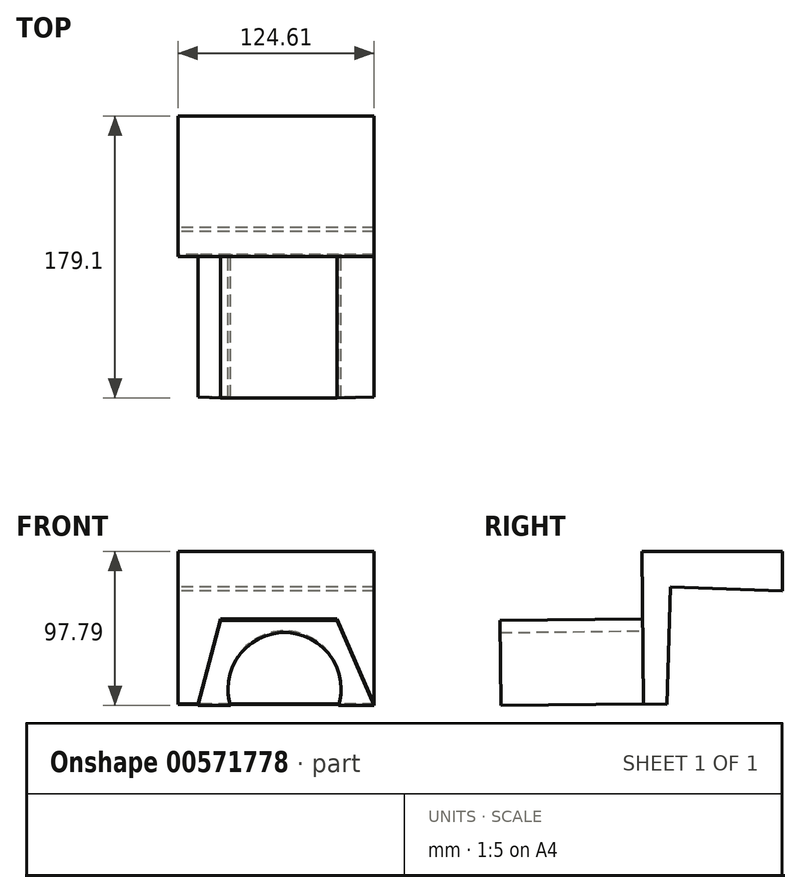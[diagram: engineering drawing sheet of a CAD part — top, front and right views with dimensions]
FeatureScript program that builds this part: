
annotation { "Feature Type Name" : "Feature", "Feature Type Description" : "" }
export const myFeature = defineFeature(function(context is Context, id is Id, definition is map)
    precondition{}
    {
        {
            var Q0;
            Q0=qCreatedBy(makeId("Right.planeOp"),FACE);
            var sketch = newSketch(context, id + "F0", { "sketchPlane" : qUnion([Q0])});
            skLineSegment(sketch, "E0", {"start": v(-40.66, 42.4) * mm, "end": v(48.47, 42.4) * mm});
            skLineSegment(sketch, "E1", {"start": v(48.47, 42.4) * mm, "end": v(48.47, 17.48) * mm});
            skLineSegment(sketch, "E2", {"start": v(48.47, 17.48) * mm, "end": v(-22.34, 19.8) * mm});
            skLineSegment(sketch, "E3", {"start": v(-22.34, 19.8) * mm, "end": v(-24.79, -54.84) * mm});
            skLineSegment(sketch, "E4", {"start": v(-24.79, -54.84) * mm, "end": v(-39.54, -54.35) * mm});
            skLineSegment(sketch, "E5", {"start": v(-39.54, -54.35) * mm, "end": v(-40.66, 42.4) * mm});
            skSolve(sketch);
        }
        {
            var Q0;
            Q0=makeQuery(id+"F0.imprint","IMPRINT",FACE,{"disambiguationData":[TD([[makeQuery(id+"F0.imprint","IMPRINT",EDGE,{"derivedFrom":sQuery(id+"F0.wireOp",EDGE,"E0")}),-1.0]])]});
            extrude(context, id + "F1", {"entities" : qUnion([Q0]), "depth" : 124.6 * mm, "offsetDistance" : 25.4 * mm});
        }
        {
            var Q0;
            Q0=makeQuery(id+"F1.opExtrude","SWEPT_FACE",FACE,{"disambiguationData":[OSD([sQuery(id+"F0.wireOp",EDGE,"E5")])]});
            var sketch = newSketch(context, id + "F2", { "sketchPlane" : qUnion([Q0])});
            skArc(sketch, "E6", {"start": v(102.07, -53.9) * mm, "mid": v(67.64, -7.56) * mm, "end": v(33.2, -53.9) * mm});
            skLineSegment(sketch, "E7", {"start": v(33.2, -53.9) * mm, "end": v(12.7, -53.9) * mm});
            skLineSegment(sketch, "E8", {"start": v(12.7, -53.9) * mm, "end": v(12.7, -53.9) * mm});
            skLineSegment(sketch, "E9", {"start": v(12.7, -53.9) * mm, "end": v(27.1, 0) * mm});
            skLineSegment(sketch, "E10", {"start": v(27.1, 0) * mm, "end": v(100.9, 0) * mm});
            skLineSegment(sketch, "E11", {"start": v(100.9, 0) * mm, "end": v(124.6, -53.9) * mm});
            skLineSegment(sketch, "E12", {"start": v(124.6, -53.9) * mm, "end": v(131.86, -62.3) * mm});
            skLineSegment(sketch, "E13", {"start": v(131.86, -62.3) * mm, "end": v(102.07, -53.9) * mm});
            skSolve(sketch);
        }
        {
            var Q0;
            {var subQ3=sQuery(id+"F2.wireOp",EDGE,"E6");Q0=makeQuery(id+"F2.imprint","IMPRINT",FACE,{"disambiguationData":[TD([[makeQuery(id+"F2.imprint","IMPRINT",EDGE,{"derivedFrom":subQ3}),-1.0]])]});}
            extrude(context, id + "F3", {"entities" : qUnion([Q0]), "operationType" : NewBodyOperationType.ADD, "depth" : 90.47 * mm, "offsetDistance" : 25.4 * mm});
        }
    });
